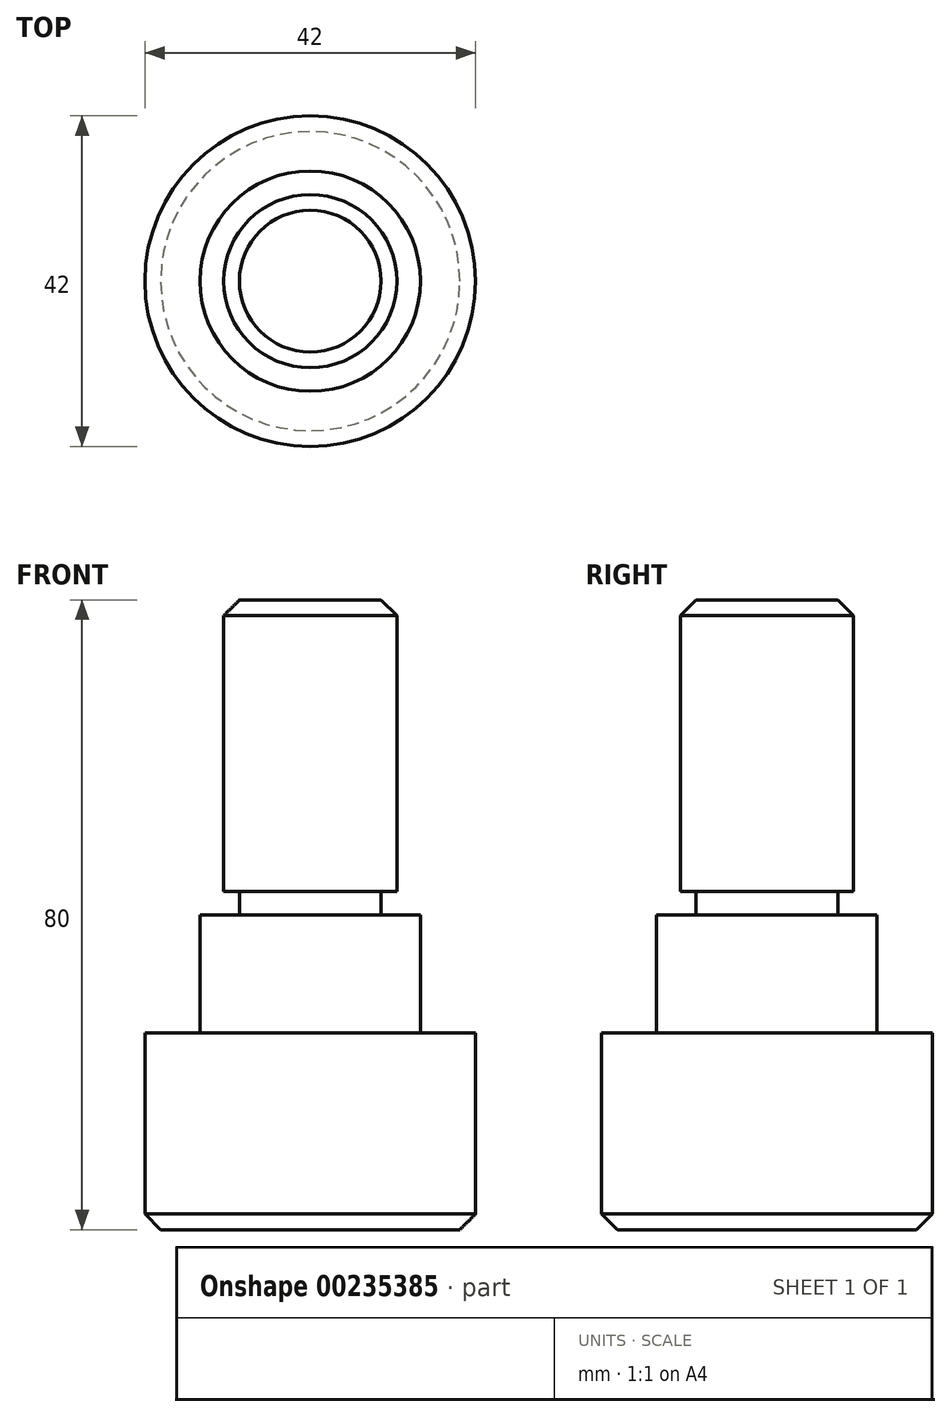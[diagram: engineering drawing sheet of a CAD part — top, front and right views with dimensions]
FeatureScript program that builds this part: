
annotation { "Feature Type Name" : "Feature", "Feature Type Description" : "" }
export const myFeature = defineFeature(function(context is Context, id is Id, definition is map)
    precondition{}
    {
        {
            var Q0;
            Q0=qCreatedBy(makeId("Front.planeOp"),FACE);
            var sketch = newSketch(context, id + "F0", { "sketchPlane" : qUnion([Q0])});
            skLineSegment(sketch, "E0", {"start": v(0, -32.43) * mm, "end": v(21, -32.43) * mm});
            skLineSegment(sketch, "E1", {"start": v(21, -32.43) * mm, "end": v(21, -7.43) * mm});
            skLineSegment(sketch, "E2", {"start": v(21, -7.43) * mm, "end": v(14, -7.43) * mm});
            skLineSegment(sketch, "E3", {"start": v(14, -7.43) * mm, "end": v(14, 7.57) * mm});
            skLineSegment(sketch, "E4", {"start": v(14, 7.57) * mm, "end": v(9, 7.57) * mm});
            skLineSegment(sketch, "E5", {"start": v(9, 7.57) * mm, "end": v(9, 10.57) * mm});
            skLineSegment(sketch, "E6", {"start": v(9, 10.57) * mm, "end": v(11, 10.57) * mm});
            skLineSegment(sketch, "E7", {"start": v(11, 10.57) * mm, "end": v(11, 47.57) * mm});
            skLineSegment(sketch, "E8", {"start": v(11, 47.57) * mm, "end": v(0, 47.57) * mm});
            skLineSegment(sketch, "E9", {"start": v(0, 47.57) * mm, "end": v(0, -32.43) * mm});
            skLineSegment(sketch, "E10", {"start": v(14, -7.43) * mm, "end": v(0, -7.43) * mm});
            skLineSegment(sketch, "E11", {"start": v(0, -7.43) * mm, "end": v(-0.04, -8.08) * mm});
            skLineSegment(sketch, "E12", {"start": v(9, 7.57) * mm, "end": v(0, 7.57) * mm});
            skLineSegment(sketch, "E13", {"start": v(9, 10.57) * mm, "end": v(0, 10.57) * mm});
            skSolve(sketch);
        }
        {
            var Q0;
            Q0=makeQuery(id+"F0.imprint","IMPRINT",FACE,{"disambiguationData":[TD([[makeQuery(id+"F0.imprint","IMPRINT",EDGE,{"derivedFrom":sQuery(id+"F0.wireOp",EDGE,"E6")}),1.0]])]});
            var Q1;
            Q1=makeQuery(id+"F0.imprint","IMPRINT",FACE,{"disambiguationData":[TD([[makeQuery(id+"F0.imprint","IMPRINT",EDGE,{"derivedFrom":sQuery(id+"F0.wireOp",EDGE,"E5")}),1.0]])]});
            var Q2;
            Q2=makeQuery(id+"F0.imprint","IMPRINT",FACE,{"disambiguationData":[TD([[makeQuery(id+"F0.imprint","IMPRINT",EDGE,{"derivedFrom":sQuery(id+"F0.wireOp",EDGE,"E3")}),1.0]])]});
            var Q3;
            {var subQ1=sQuery(id+"F0.wireOp",EDGE,"E0");Q3=makeQuery(id+"F0.imprint","IMPRINT",FACE,{"disambiguationData":[TD([[makeQuery(id+"F0.imprint","IMPRINT",EDGE,{"derivedFrom":subQ1}),1.0]])]});}
            var Q4;
            Q4=sQuery(id+"F0.wireOp",EDGE,"E9");
            revolve(context, id + "F1", {"entities" : qUnion([Q0, Q1, Q2, Q3]), "axis" : qUnion([Q4]), "revolveType" : RevolveType.FULL});
        }
        {
            var Q0;
            Q0=makeQuery(id+"F1.opRevolve","SWEPT_EDGE",EDGE,{"disambiguationData":[OSD([sQuery(id+"F0.wireOp",EDGE,"E7"),sQuery(id+"F0.wireOp",EDGE,"E8")])]});
            var Q1;
            Q1=makeQuery(id+"F1.opRevolve","SWEPT_EDGE",EDGE,{"disambiguationData":[OSD([sQuery(id+"F0.wireOp",EDGE,"E0"),sQuery(id+"F0.wireOp",EDGE,"E1")])]});
            chamfer(context, id + "F2", {"entities" : qUnion([Q0, Q1]), "chamferType" : ChamferType.OFFSET_ANGLE, "width" : 2 * mm, "oppositeDirection" : false, "angle" : 45 * degree, "tangentPropagation" : true});
        }
    });
